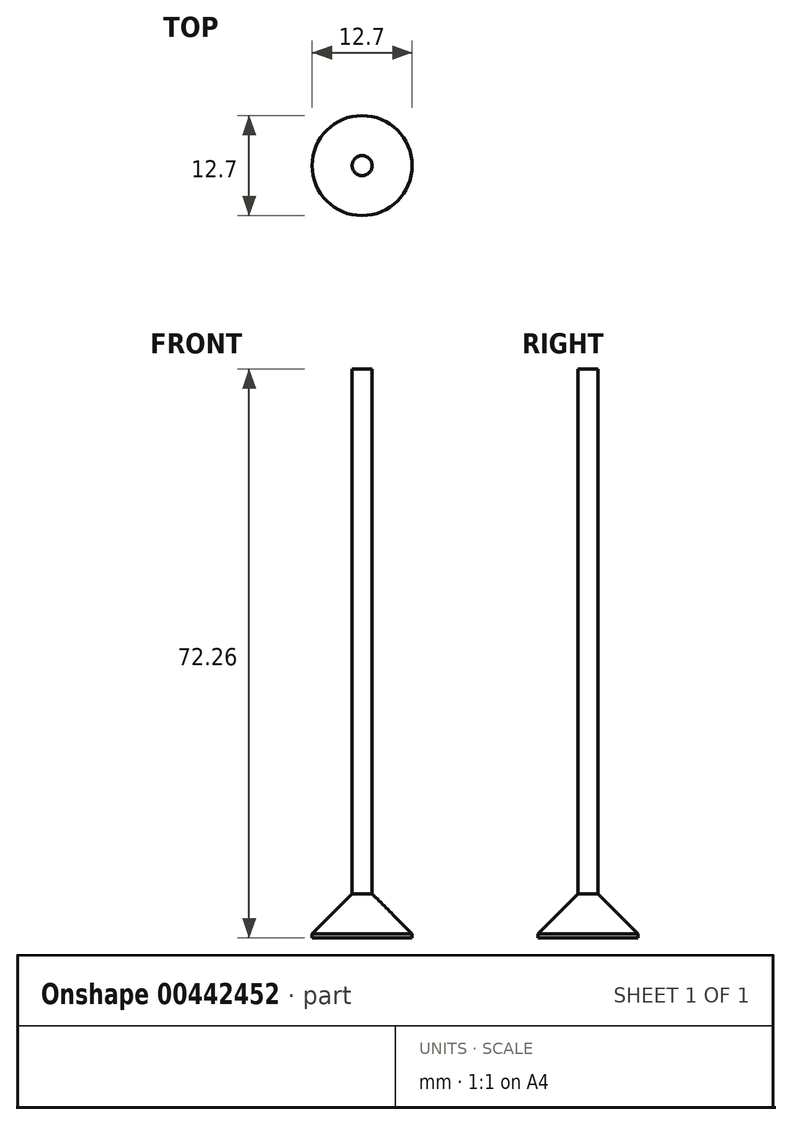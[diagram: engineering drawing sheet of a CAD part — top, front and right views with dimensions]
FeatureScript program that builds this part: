
annotation { "Feature Type Name" : "Feature", "Feature Type Description" : "" }
export const myFeature = defineFeature(function(context is Context, id is Id, definition is map)
    precondition{}
    {
        {
            var Q0;
            Q0=qCreatedBy(makeId("Top.planeOp"),FACE);
            var sketch = newSketch(context, id + "F0", { "sketchPlane" : qUnion([Q0])});
            skCircle(sketch, "E0", {"center": v(0, 0) * mm, "radius": 6.35 * mm});
            skSolve(sketch);
        }
        {
            var Q0;
            Q0 = qSketchRegion(id + "F0", true);
            extrude(context, id + "F1", {"entities" : qUnion([Q0]), "depth" : 5.6 * mm});
        }
        {
            var Q0;
            Q0=makeQuery(id+"F1.opExtrude","CAP_EDGE",EDGE,{"disambiguationData":[OSD([sQuery(id+"F0.wireOp",EDGE,"E0")])],"isStart":false});
            chamfer(context, id + "F2", {"entities" : qUnion([Q0]), "width" : 5.08 * mm, "tangentPropagation" : true});
        }
        {
            var Q0;
            Q0=makeQuery(id+"F1.opExtrude","CAP_FACE",FACE,{"disambiguationData":[OSD([sQuery(id+"F0.wireOp",EDGE,"E0")])],"isStart":false});
            extrude(context, id + "F3", {"entities" : qUnion([Q0]), "operationType" : NewBodyOperationType.ADD, "depth" : 66.67 * mm});
        }
    });
